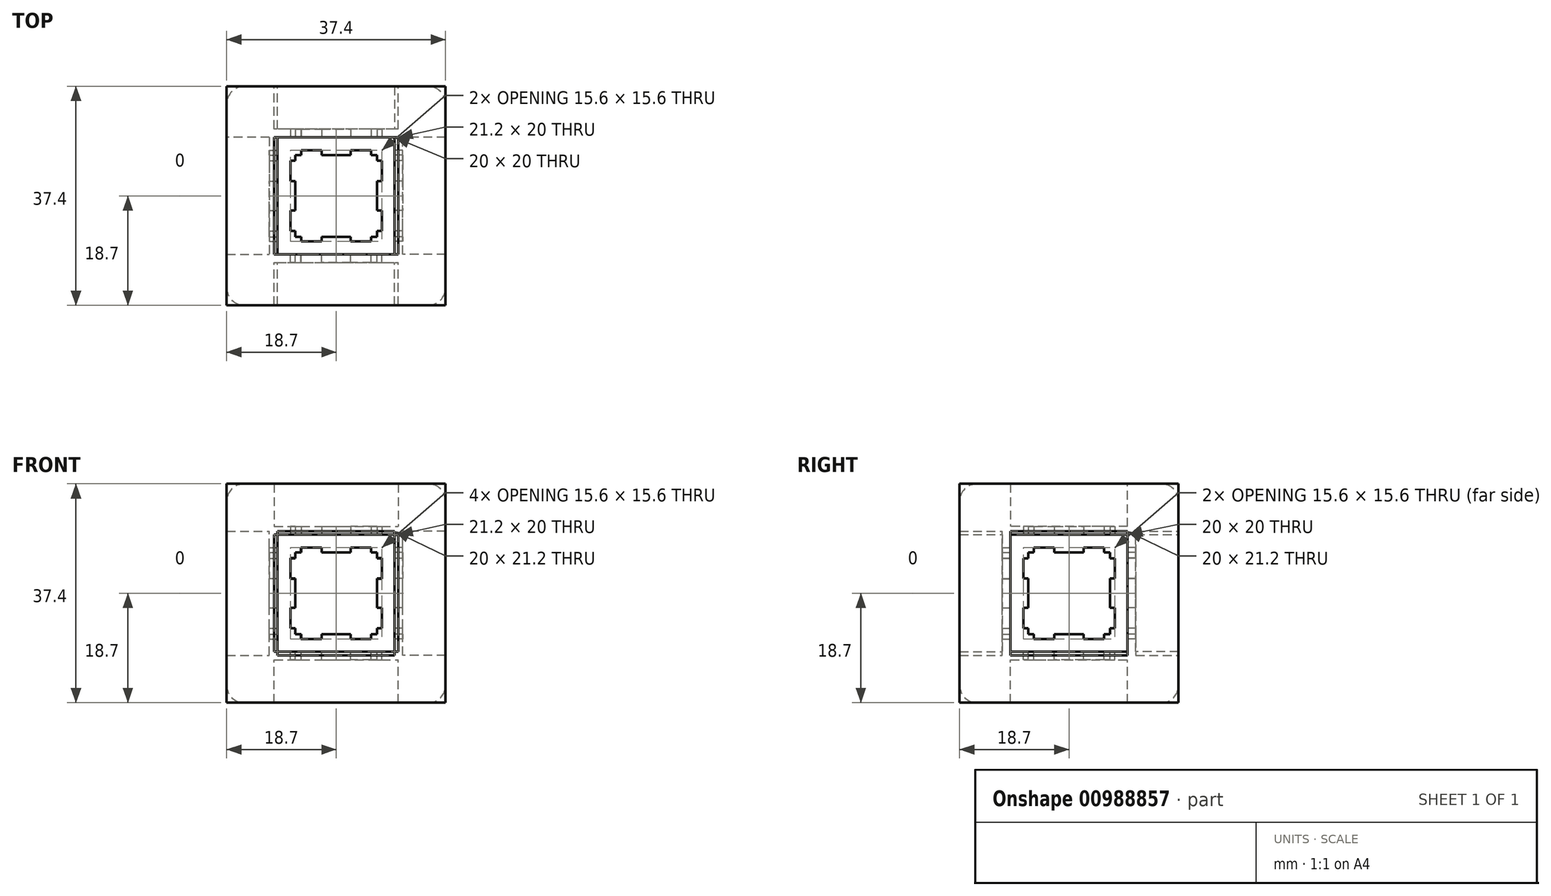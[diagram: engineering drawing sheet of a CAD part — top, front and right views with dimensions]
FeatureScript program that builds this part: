
annotation { "Feature Type Name" : "Feature", "Feature Type Description" : "" }
export const myFeature = defineFeature(function(context is Context, id is Id, definition is map)
    precondition{}
    {
        {
            var Q0;
            Q0=qCreatedBy(makeId("Top.planeOp"),FACE);
            var sketch = newSketch(context, id + "F0", { "sketchPlane" : qUnion([Q0])});
            skLineSegment(sketch, "E0.right", {"start": v(-6.98, -6.99) * mm, "end": v(-6.98, -6) * mm});
            skPoint(sketch, "E0.middle", {"position": v(0, 0) * mm});
            skLineSegment(sketch, "E1", {"start": v(-6.98, -6) * mm, "end": v(-7.8, -6) * mm});
            skLineSegment(sketch, "E2", {"start": v(-6.98, -2.5) * mm, "end": v(-7.8, -2.5) * mm});
            skLineSegment(sketch, "E3.trimOffspring", {"start": v(-6.98, -2.5) * mm, "end": v(-6.98, 0) * mm});
            skLineSegment(sketch, "E4.trimOffspring", {"start": v(-7.8, -6) * mm, "end": v(-7.8, -2.5) * mm});
            skLineSegment(sketch, "E5.MirrorCS", {"start": v(-2.5, -6.99) * mm, "end": v(0, -6.99) * mm});
            skLineSegment(sketch, "E6.MirrorCS", {"start": v(-2.5, -6.99) * mm, "end": v(-2.5, -7.8) * mm});
            skLineSegment(sketch, "E7.MirrorCS", {"start": v(-5.98, -7.8) * mm, "end": v(-2.48, -7.8) * mm});
            skLineSegment(sketch, "E8.MirrorCS", {"start": v(-5.98, -6.99) * mm, "end": v(-5.98, -7.8) * mm});
            skLineSegment(sketch, "E9.MirrorCS", {"start": v(-6.98, -6.99) * mm, "end": v(-5.98, -6.99) * mm});
            skLineSegment(sketch, "E10.MirrorCS", {"start": v(2.5, -6.99) * mm, "end": v(2.5, -7.8) * mm});
            skLineSegment(sketch, "E11.MirrorCS", {"start": v(6.98, -6.99) * mm, "end": v(5.98, -6.99) * mm});
            skLineSegment(sketch, "E12.MirrorCS", {"start": v(5.98, -7.8) * mm, "end": v(2.48, -7.8) * mm});
            skLineSegment(sketch, "E13.MirrorCS", {"start": v(7.8, -6) * mm, "end": v(7.8, -2.5) * mm});
            skLineSegment(sketch, "E14.MirrorCS", {"start": v(6.98, -6.99) * mm, "end": v(6.98, -6) * mm});
            skLineSegment(sketch, "E15.MirrorCS", {"start": v(6.98, -2.5) * mm, "end": v(6.98, 0) * mm});
            skLineSegment(sketch, "E16.MirrorCS", {"start": v(6.98, -2.5) * mm, "end": v(7.8, -2.5) * mm});
            skLineSegment(sketch, "E17.MirrorCS", {"start": v(6.98, -6) * mm, "end": v(7.8, -6) * mm});
            skLineSegment(sketch, "E18.MirrorCS", {"start": v(5.98, -6.99) * mm, "end": v(5.98, -7.8) * mm});
            skLineSegment(sketch, "E19.MirrorCS", {"start": v(2.5, -6.99) * mm, "end": v(0, -6.99) * mm});
            skLineSegment(sketch, "E20.MirrorCS", {"start": v(6.98, 6.99) * mm, "end": v(5.98, 6.99) * mm});
            skLineSegment(sketch, "E21.MirrorCS", {"start": v(2.5, 6.99) * mm, "end": v(0, 6.99) * mm});
            skLineSegment(sketch, "E22.MirrorCS", {"start": v(6.98, 2.5) * mm, "end": v(7.8, 2.5) * mm});
            skLineSegment(sketch, "E23.MirrorCS", {"start": v(-6.98, 6.99) * mm, "end": v(-6.98, 6) * mm});
            skLineSegment(sketch, "E24.MirrorCS", {"start": v(-6.98, 6) * mm, "end": v(-7.8, 6) * mm});
            skLineSegment(sketch, "E25.MirrorCS", {"start": v(-7.8, 6) * mm, "end": v(-7.8, 2.5) * mm});
            skLineSegment(sketch, "E26.MirrorCS", {"start": v(6.98, 6.99) * mm, "end": v(6.98, 6) * mm});
            skLineSegment(sketch, "E27.MirrorCS", {"start": v(-2.5, 6.99) * mm, "end": v(-2.5, 7.8) * mm});
            skLineSegment(sketch, "E28.MirrorCS", {"start": v(-6.98, 2.5) * mm, "end": v(-6.98, 0) * mm});
            skLineSegment(sketch, "E29.MirrorCS", {"start": v(-5.98, 6.99) * mm, "end": v(-5.98, 7.8) * mm});
            skLineSegment(sketch, "E30.MirrorCS", {"start": v(-5.98, 7.8) * mm, "end": v(-2.48, 7.8) * mm});
            skLineSegment(sketch, "E31.MirrorCS", {"start": v(-2.5, 6.99) * mm, "end": v(0, 6.99) * mm});
            skLineSegment(sketch, "E32.MirrorCS", {"start": v(2.5, 6.99) * mm, "end": v(2.5, 7.8) * mm});
            skLineSegment(sketch, "E33.MirrorCS", {"start": v(6.98, 2.5) * mm, "end": v(6.98, 0) * mm});
            skLineSegment(sketch, "E34.MirrorCS", {"start": v(5.98, 7.8) * mm, "end": v(2.48, 7.8) * mm});
            skLineSegment(sketch, "E35.MirrorCS", {"start": v(-6.98, 2.5) * mm, "end": v(-7.8, 2.5) * mm});
            skLineSegment(sketch, "E36.MirrorCS", {"start": v(7.8, 6) * mm, "end": v(7.8, 2.5) * mm});
            skLineSegment(sketch, "E37.MirrorCS", {"start": v(-6.98, 6.99) * mm, "end": v(-5.98, 6.99) * mm});
            skLineSegment(sketch, "E38.MirrorCS", {"start": v(5.98, 6.99) * mm, "end": v(5.98, 7.8) * mm});
            skLineSegment(sketch, "E39.MirrorCS", {"start": v(6.98, 6) * mm, "end": v(7.8, 6) * mm});
            skLineSegment(sketch, "E40.bottom", {"start": v(10.6, 10.6) * mm, "end": v(-10.6, 10.6) * mm});
            skLineSegment(sketch, "E40.top", {"start": v(10.6, -10.6) * mm, "end": v(-10.6, -10.6) * mm});
            skLineSegment(sketch, "E40.left", {"start": v(10.6, 10.6) * mm, "end": v(10.6, -10.6) * mm});
            skLineSegment(sketch, "E40.right", {"start": v(-10.6, 10.6) * mm, "end": v(-10.6, -10.6) * mm});
            skLineSegment(sketch, "E41.bottom", {"start": v(18.7, 18.7) * mm, "end": v(-18.7, 18.7) * mm});
            skLineSegment(sketch, "E41.top", {"start": v(18.7, -18.7) * mm, "end": v(-18.7, -18.7) * mm});
            skLineSegment(sketch, "E41.left", {"start": v(18.7, 18.7) * mm, "end": v(18.7, -18.7) * mm});
            skLineSegment(sketch, "E41.right", {"start": v(-18.7, 18.7) * mm, "end": v(-18.7, -18.7) * mm});
            skSolve(sketch);
        }
        {
            var Q0;
            Q0=makeQuery(id+"F0.imprint","IMPRINT",FACE,{"disambiguationData":[TD([[makeQuery(id+"F0.imprint","IMPRINT",EDGE,{"derivedFrom":sQuery(id+"F0.wireOp",EDGE,"E0.right")}),1.0]])]});
            extrude(context, id + "F1", {"entities" : qUnion([Q0]), "depth" : 1.4 * mm, "offsetDistance" : 25 * mm});
        }
        {
            var Q0;
            Q0=makeQuery(id+"F0.imprint","IMPRINT",FACE,{"disambiguationData":[TD([[makeQuery(id+"F0.imprint","IMPRINT",EDGE,{"derivedFrom":sQuery(id+"F0.wireOp",EDGE,"E40.bottom")}),-1.0]])]});
            extrude(context, id + "F2", {"entities" : qUnion([Q0]), "operationType" : NewBodyOperationType.ADD, "depth" : 8.7 * mm, "offsetDistance" : 25 * mm});
        }
        {
            var Q0;
            Q0=makeQuery(id+"F1.opExtrude","SWEPT_BODY",BODY,{"disambiguationData":[OSD([sQuery(id+"F0.wireOp",EDGE,"E0.right"),sQuery(id+"F0.wireOp",EDGE,"E1"),sQuery(id+"F0.wireOp",EDGE,"E2"),sQuery(id+"F0.wireOp",EDGE,"E3.trimOffspring"),sQuery(id+"F0.wireOp",EDGE,"E4.trimOffspring"),sQuery(id+"F0.wireOp",EDGE,"E5.MirrorCS"),sQuery(id+"F0.wireOp",EDGE,"E6.MirrorCS"),sQuery(id+"F0.wireOp",EDGE,"E7.MirrorCS"),sQuery(id+"F0.wireOp",EDGE,"E8.MirrorCS"),sQuery(id+"F0.wireOp",EDGE,"E9.MirrorCS"),sQuery(id+"F0.wireOp",EDGE,"E10.MirrorCS"),sQuery(id+"F0.wireOp",EDGE,"E11.MirrorCS"),sQuery(id+"F0.wireOp",EDGE,"E12.MirrorCS"),sQuery(id+"F0.wireOp",EDGE,"E13.MirrorCS"),sQuery(id+"F0.wireOp",EDGE,"E14.MirrorCS"),sQuery(id+"F0.wireOp",EDGE,"E15.MirrorCS"),sQuery(id+"F0.wireOp",EDGE,"E16.MirrorCS"),sQuery(id+"F0.wireOp",EDGE,"E17.MirrorCS"),sQuery(id+"F0.wireOp",EDGE,"E18.MirrorCS"),sQuery(id+"F0.wireOp",EDGE,"E19.MirrorCS"),sQuery(id+"F0.wireOp",EDGE,"E20.MirrorCS"),sQuery(id+"F0.wireOp",EDGE,"E21.MirrorCS"),sQuery(id+"F0.wireOp",EDGE,"E22.MirrorCS"),sQuery(id+"F0.wireOp",EDGE,"E23.MirrorCS"),sQuery(id+"F0.wireOp",EDGE,"E24.MirrorCS"),sQuery(id+"F0.wireOp",EDGE,"E25.MirrorCS"),sQuery(id+"F0.wireOp",EDGE,"E26.MirrorCS"),sQuery(id+"F0.wireOp",EDGE,"E27.MirrorCS"),sQuery(id+"F0.wireOp",EDGE,"E28.MirrorCS"),sQuery(id+"F0.wireOp",EDGE,"E29.MirrorCS"),sQuery(id+"F0.wireOp",EDGE,"E30.MirrorCS"),sQuery(id+"F0.wireOp",EDGE,"E31.MirrorCS"),sQuery(id+"F0.wireOp",EDGE,"E32.MirrorCS"),sQuery(id+"F0.wireOp",EDGE,"E33.MirrorCS"),sQuery(id+"F0.wireOp",EDGE,"E34.MirrorCS"),sQuery(id+"F0.wireOp",EDGE,"E35.MirrorCS"),sQuery(id+"F0.wireOp",EDGE,"E36.MirrorCS"),sQuery(id+"F0.wireOp",EDGE,"E37.MirrorCS"),sQuery(id+"F0.wireOp",EDGE,"E38.MirrorCS"),sQuery(id+"F0.wireOp",EDGE,"E39.MirrorCS"),sQuery(id+"F0.wireOp",EDGE,"E40.bottom"),sQuery(id+"F0.wireOp",EDGE,"E40.top"),sQuery(id+"F0.wireOp",EDGE,"E40.left"),sQuery(id+"F0.wireOp",EDGE,"E40.right")])]});
            transform(context, id + "F3", {"entities" : qUnion([Q0]), "transformType" : TransformType.TRANSLATION_3D, "dx" : 0 * mm, "dy" : 0 * mm, "dz" : 10 * mm, "makeCopy" : false});
        }
        {
            var Q0;
            Q0=qCreatedBy(makeId("Top.planeOp"),FACE);
            var sketch = newSketch(context, id + "F4", { "sketchPlane" : qUnion([Q0])});
            skLineSegment(sketch, "E42", {"start": v(-40.96, 0) * mm, "end": v(39.65, 0) * mm, "construction": true});
            skSolve(sketch);
        }
        {
            var Q0;
            Q0=makeQuery(id+"F1.opExtrude","SWEPT_BODY",BODY,{"disambiguationData":[OSD([sQuery(id+"F0.wireOp",EDGE,"E0.right"),sQuery(id+"F0.wireOp",EDGE,"E1"),sQuery(id+"F0.wireOp",EDGE,"E2"),sQuery(id+"F0.wireOp",EDGE,"E3.trimOffspring"),sQuery(id+"F0.wireOp",EDGE,"E4.trimOffspring"),sQuery(id+"F0.wireOp",EDGE,"E5.MirrorCS"),sQuery(id+"F0.wireOp",EDGE,"E6.MirrorCS"),sQuery(id+"F0.wireOp",EDGE,"E7.MirrorCS"),sQuery(id+"F0.wireOp",EDGE,"E8.MirrorCS"),sQuery(id+"F0.wireOp",EDGE,"E9.MirrorCS"),sQuery(id+"F0.wireOp",EDGE,"E10.MirrorCS"),sQuery(id+"F0.wireOp",EDGE,"E11.MirrorCS"),sQuery(id+"F0.wireOp",EDGE,"E12.MirrorCS"),sQuery(id+"F0.wireOp",EDGE,"E13.MirrorCS"),sQuery(id+"F0.wireOp",EDGE,"E14.MirrorCS"),sQuery(id+"F0.wireOp",EDGE,"E15.MirrorCS"),sQuery(id+"F0.wireOp",EDGE,"E16.MirrorCS"),sQuery(id+"F0.wireOp",EDGE,"E17.MirrorCS"),sQuery(id+"F0.wireOp",EDGE,"E18.MirrorCS"),sQuery(id+"F0.wireOp",EDGE,"E19.MirrorCS"),sQuery(id+"F0.wireOp",EDGE,"E20.MirrorCS"),sQuery(id+"F0.wireOp",EDGE,"E21.MirrorCS"),sQuery(id+"F0.wireOp",EDGE,"E22.MirrorCS"),sQuery(id+"F0.wireOp",EDGE,"E23.MirrorCS"),sQuery(id+"F0.wireOp",EDGE,"E24.MirrorCS"),sQuery(id+"F0.wireOp",EDGE,"E25.MirrorCS"),sQuery(id+"F0.wireOp",EDGE,"E26.MirrorCS"),sQuery(id+"F0.wireOp",EDGE,"E27.MirrorCS"),sQuery(id+"F0.wireOp",EDGE,"E28.MirrorCS"),sQuery(id+"F0.wireOp",EDGE,"E29.MirrorCS"),sQuery(id+"F0.wireOp",EDGE,"E30.MirrorCS"),sQuery(id+"F0.wireOp",EDGE,"E31.MirrorCS"),sQuery(id+"F0.wireOp",EDGE,"E32.MirrorCS"),sQuery(id+"F0.wireOp",EDGE,"E33.MirrorCS"),sQuery(id+"F0.wireOp",EDGE,"E34.MirrorCS"),sQuery(id+"F0.wireOp",EDGE,"E35.MirrorCS"),sQuery(id+"F0.wireOp",EDGE,"E36.MirrorCS"),sQuery(id+"F0.wireOp",EDGE,"E37.MirrorCS"),sQuery(id+"F0.wireOp",EDGE,"E38.MirrorCS"),sQuery(id+"F0.wireOp",EDGE,"E39.MirrorCS"),sQuery(id+"F0.wireOp",EDGE,"E40.bottom"),sQuery(id+"F0.wireOp",EDGE,"E40.top"),sQuery(id+"F0.wireOp",EDGE,"E40.left"),sQuery(id+"F0.wireOp",EDGE,"E40.right")])]});
            var Q1;
            Q1=sQuery(id+"F4.wireOp",EDGE,"E42");
            circularPattern(context, id + "F5", {"operationType" : NewBodyOperationType.ADD, "entities" : qUnion([Q0]), "axis" : qUnion([Q1]), "angle" : 360 * degree, "instanceCount" : 4, "equalSpace" : true});
        }
        {
            var Q0;
            Q0=qCreatedBy(makeId("Right.planeOp"),FACE);
            var sketch = newSketch(context, id + "F6", { "sketchPlane" : qUnion([Q0])});
            skLineSegment(sketch, "E43", {"start": v(45.1, 0) * mm, "end": v(-29.25, 0) * mm, "construction": true});
            skSolve(sketch);
        }
        {
            var Q0;
            Q0=makeQuery(id+"F1.opExtrude","SWEPT_BODY",BODY,{"disambiguationData":[OSD([sQuery(id+"F0.wireOp",EDGE,"E0.right"),sQuery(id+"F0.wireOp",EDGE,"E1"),sQuery(id+"F0.wireOp",EDGE,"E2"),sQuery(id+"F0.wireOp",EDGE,"E3.trimOffspring"),sQuery(id+"F0.wireOp",EDGE,"E4.trimOffspring"),sQuery(id+"F0.wireOp",EDGE,"E5.MirrorCS"),sQuery(id+"F0.wireOp",EDGE,"E6.MirrorCS"),sQuery(id+"F0.wireOp",EDGE,"E7.MirrorCS"),sQuery(id+"F0.wireOp",EDGE,"E8.MirrorCS"),sQuery(id+"F0.wireOp",EDGE,"E9.MirrorCS"),sQuery(id+"F0.wireOp",EDGE,"E10.MirrorCS"),sQuery(id+"F0.wireOp",EDGE,"E11.MirrorCS"),sQuery(id+"F0.wireOp",EDGE,"E12.MirrorCS"),sQuery(id+"F0.wireOp",EDGE,"E13.MirrorCS"),sQuery(id+"F0.wireOp",EDGE,"E14.MirrorCS"),sQuery(id+"F0.wireOp",EDGE,"E15.MirrorCS"),sQuery(id+"F0.wireOp",EDGE,"E16.MirrorCS"),sQuery(id+"F0.wireOp",EDGE,"E17.MirrorCS"),sQuery(id+"F0.wireOp",EDGE,"E18.MirrorCS"),sQuery(id+"F0.wireOp",EDGE,"E19.MirrorCS"),sQuery(id+"F0.wireOp",EDGE,"E20.MirrorCS"),sQuery(id+"F0.wireOp",EDGE,"E21.MirrorCS"),sQuery(id+"F0.wireOp",EDGE,"E22.MirrorCS"),sQuery(id+"F0.wireOp",EDGE,"E23.MirrorCS"),sQuery(id+"F0.wireOp",EDGE,"E24.MirrorCS"),sQuery(id+"F0.wireOp",EDGE,"E25.MirrorCS"),sQuery(id+"F0.wireOp",EDGE,"E26.MirrorCS"),sQuery(id+"F0.wireOp",EDGE,"E27.MirrorCS"),sQuery(id+"F0.wireOp",EDGE,"E28.MirrorCS"),sQuery(id+"F0.wireOp",EDGE,"E29.MirrorCS"),sQuery(id+"F0.wireOp",EDGE,"E30.MirrorCS"),sQuery(id+"F0.wireOp",EDGE,"E31.MirrorCS"),sQuery(id+"F0.wireOp",EDGE,"E32.MirrorCS"),sQuery(id+"F0.wireOp",EDGE,"E33.MirrorCS"),sQuery(id+"F0.wireOp",EDGE,"E34.MirrorCS"),sQuery(id+"F0.wireOp",EDGE,"E35.MirrorCS"),sQuery(id+"F0.wireOp",EDGE,"E36.MirrorCS"),sQuery(id+"F0.wireOp",EDGE,"E37.MirrorCS"),sQuery(id+"F0.wireOp",EDGE,"E38.MirrorCS"),sQuery(id+"F0.wireOp",EDGE,"E39.MirrorCS"),sQuery(id+"F0.wireOp",EDGE,"E40.bottom"),sQuery(id+"F0.wireOp",EDGE,"E40.top"),sQuery(id+"F0.wireOp",EDGE,"E40.left"),sQuery(id+"F0.wireOp",EDGE,"E40.right")])]});
            var Q1;
            Q1=sQuery(id+"F6.wireOp",EDGE,"E43");
            transform(context, id + "F7", {"entities" : qUnion([Q0]), "transformType" : TransformType.ROTATION, "transformAxis" : qUnion([Q1]), "angle" : 90 * degree, "makeCopy" : true});
        }
        {
            var Q0;
            {var subQ0=sQuery(id+"F0.wireOp",EDGE,"E41.right");Q0=makeQuery(id+"F5.boolean.opBoolean","MERGE",EDGE,{"derivedFrom":[makeQuery(id+"F2.opExtrude","SWEPT_EDGE",EDGE,{"disambiguationData":[OSD([sQuery(id+"F0.wireOp",EDGE,"E41.bottom"),subQ0])]}),makeQuery(id+"F5.opPattern","COPY",EDGE,{"derivedFrom":makeQuery(id+"F2.opExtrude","SWEPT_EDGE",EDGE,{"disambiguationData":[OSD([sQuery(id+"F0.wireOp",EDGE,"E41.top"),subQ0])]}),"instanceName":"2"}),makeQuery(id+"F5.opPattern","COPY",EDGE,{"derivedFrom":makeQuery(id+"F2.opExtrude","CAP_EDGE",EDGE,{"disambiguationData":[OSD([subQ0])],"isStart":false}),"instanceName":"3"})]});}
            var Q1;
            Q1=makeQuery(id+"F5.opPattern","COPY",EDGE,{"derivedFrom":makeQuery(id+"F2.opExtrude","CAP_EDGE",EDGE,{"disambiguationData":[OSD([sQuery(id+"F0.wireOp",EDGE,"E41.top")])],"isStart":false}),"instanceName":"2"});
            var Q2;
            Q2=makeQuery(id+"F2.opExtrude","CAP_EDGE",EDGE,{"disambiguationData":[OSD([sQuery(id+"F0.wireOp",EDGE,"E41.bottom")])],"isStart":false});
            var Q3;
            {var subQ0=sQuery(id+"F0.wireOp",EDGE,"E41.left");Q3=makeQuery(id+"F5.boolean.opBoolean","MERGE",EDGE,{"derivedFrom":[makeQuery(id+"F2.opExtrude","SWEPT_EDGE",EDGE,{"disambiguationData":[OSD([sQuery(id+"F0.wireOp",EDGE,"E41.bottom"),subQ0])]}),makeQuery(id+"F5.opPattern","COPY",EDGE,{"derivedFrom":makeQuery(id+"F2.opExtrude","SWEPT_EDGE",EDGE,{"disambiguationData":[OSD([sQuery(id+"F0.wireOp",EDGE,"E41.top"),subQ0])]}),"instanceName":"2"}),makeQuery(id+"F5.opPattern","COPY",EDGE,{"derivedFrom":makeQuery(id+"F2.opExtrude","CAP_EDGE",EDGE,{"disambiguationData":[OSD([subQ0])],"isStart":false}),"instanceName":"3"})]});}
            var Q4;
            Q4=makeQuery(id+"F2.opExtrude","CAP_EDGE",EDGE,{"disambiguationData":[OSD([sQuery(id+"F0.wireOp",EDGE,"E41.left")])],"isStart":false});
            var Q5;
            Q5=makeQuery(id+"F2.opExtrude","CAP_EDGE",EDGE,{"disambiguationData":[OSD([sQuery(id+"F0.wireOp",EDGE,"E41.right")])],"isStart":false});
            var Q6;
            {var subQ0=sQuery(id+"F0.wireOp",EDGE,"E41.right");Q6=makeQuery(id+"F5.boolean.opBoolean","MERGE",EDGE,{"derivedFrom":[makeQuery(id+"F5.opPattern","COPY",EDGE,{"derivedFrom":makeQuery(id+"F2.opExtrude","SWEPT_EDGE",EDGE,{"disambiguationData":[OSD([sQuery(id+"F0.wireOp",EDGE,"E41.top"),subQ0])]}),"instanceName":"1"}),makeQuery(id+"F5.opPattern","COPY",EDGE,{"derivedFrom":makeQuery(id+"F2.opExtrude","CAP_EDGE",EDGE,{"disambiguationData":[OSD([subQ0])],"isStart":false}),"instanceName":"2"})]});}
            var Q7;
            {var subQ0=sQuery(id+"F0.wireOp",EDGE,"E41.left");Q7=makeQuery(id+"F5.boolean.opBoolean","MERGE",EDGE,{"derivedFrom":[makeQuery(id+"F5.opPattern","COPY",EDGE,{"derivedFrom":makeQuery(id+"F2.opExtrude","SWEPT_EDGE",EDGE,{"disambiguationData":[OSD([sQuery(id+"F0.wireOp",EDGE,"E41.top"),subQ0])]}),"instanceName":"1"}),makeQuery(id+"F5.opPattern","COPY",EDGE,{"derivedFrom":makeQuery(id+"F2.opExtrude","CAP_EDGE",EDGE,{"disambiguationData":[OSD([subQ0])],"isStart":false}),"instanceName":"2"})]});}
            var Q8;
            Q8=makeQuery(id+"F5.opPattern","COPY",EDGE,{"derivedFrom":makeQuery(id+"F2.opExtrude","CAP_EDGE",EDGE,{"disambiguationData":[OSD([sQuery(id+"F0.wireOp",EDGE,"E41.top")])],"isStart":false}),"instanceName":"1"});
            var Q9;
            {var subQ0=sQuery(id+"F0.wireOp",EDGE,"E41.left");Q9=makeQuery(id+"F5.boolean.opBoolean","MERGE",EDGE,{"derivedFrom":[makeQuery(id+"F2.opExtrude","SWEPT_EDGE",EDGE,{"disambiguationData":[OSD([sQuery(id+"F0.wireOp",EDGE,"E41.top"),subQ0])]}),makeQuery(id+"F5.opPattern","COPY",EDGE,{"derivedFrom":makeQuery(id+"F2.opExtrude","CAP_EDGE",EDGE,{"disambiguationData":[OSD([subQ0])],"isStart":false}),"instanceName":"1"})]});}
            var Q10;
            Q10=makeQuery(id+"F2.opExtrude","CAP_EDGE",EDGE,{"disambiguationData":[OSD([sQuery(id+"F0.wireOp",EDGE,"E41.top")])],"isStart":false});
            var Q11;
            {var subQ0=sQuery(id+"F0.wireOp",EDGE,"E41.right");Q11=makeQuery(id+"F5.boolean.opBoolean","MERGE",EDGE,{"derivedFrom":[makeQuery(id+"F2.opExtrude","SWEPT_EDGE",EDGE,{"disambiguationData":[OSD([sQuery(id+"F0.wireOp",EDGE,"E41.top"),subQ0])]}),makeQuery(id+"F5.opPattern","COPY",EDGE,{"derivedFrom":makeQuery(id+"F2.opExtrude","CAP_EDGE",EDGE,{"disambiguationData":[OSD([subQ0])],"isStart":false}),"instanceName":"1"})]});}
            fillet(context, id + "F8", {"entities" : qUnion([Q0, Q1, Q2, Q3, Q4, Q5, Q6, Q7, Q8, Q9, Q10, Q11]), "radius" : 3 * mm, "tangentPropagation" : true, "allowEdgeOverflow" : false});
        }
    });
